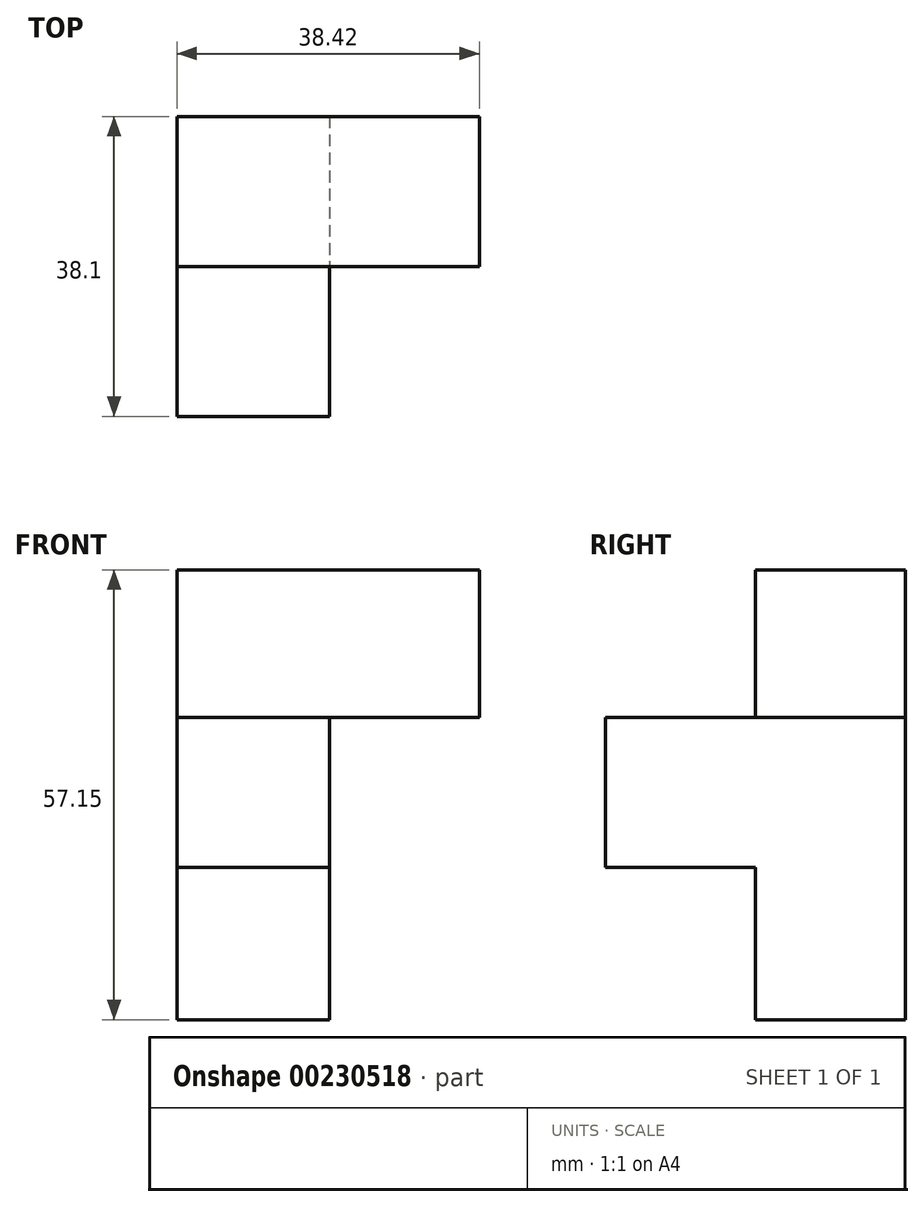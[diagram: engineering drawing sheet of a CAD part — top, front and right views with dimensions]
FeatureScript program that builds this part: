
annotation { "Feature Type Name" : "Feature", "Feature Type Description" : "" }
export const myFeature = defineFeature(function(context is Context, id is Id, definition is map)
    precondition{}
    {
        {
            var Q0;
            Q0=qCreatedBy(makeId("Top.planeOp"),FACE);
            var sketch = newSketch(context, id + "F0", { "sketchPlane" : qUnion([Q0])});
            skLineSegment(sketch, "E0.bottom", {"start": v(-19.07, -38.1) * mm, "end": v(-38.44, -38.1) * mm});
            skLineSegment(sketch, "E0.top", {"start": v(-19.07, -19.05) * mm, "end": v(-38.44, -19.05) * mm});
            skLineSegment(sketch, "E0.left", {"start": v(-19.07, -38.1) * mm, "end": v(-19.07, -19.05) * mm});
            skLineSegment(sketch, "E0.right", {"start": v(-38.44, -38.1) * mm, "end": v(-38.44, -19.05) * mm});
            skSolve(sketch);
        }
        {
            var Q0;
            Q0=makeQuery(id+"F0.imprint","IMPRINT",FACE,{"disambiguationData":[TD([[makeQuery(id+"F0.imprint","IMPRINT",EDGE,{"derivedFrom":sQuery(id+"F0.wireOp",EDGE,"E0.bottom")}),-1.0]])]});
            extrude(context, id + "F1", {"entities" : qUnion([Q0]), "depth" : 57.15 * mm});
        }
        {
            var Q0;
            Q0=makeQuery(id+"F1.opExtrude","SWEPT_FACE",FACE,{"disambiguationData":[OSD([sQuery(id+"F0.wireOp",EDGE,"E0.bottom")])]});
            var sketch = newSketch(context, id + "F2", { "sketchPlane" : qUnion([Q0])});
            skLineSegment(sketch, "E1.bottom", {"start": v(-19.07, 38.4) * mm, "end": v(-38.44, 38.4) * mm});
            skLineSegment(sketch, "E1.top", {"start": v(-19.07, 19.34) * mm, "end": v(-38.44, 19.34) * mm});
            skLineSegment(sketch, "E1.left", {"start": v(-19.07, 38.4) * mm, "end": v(-19.07, 19.34) * mm});
            skLineSegment(sketch, "E1.right", {"start": v(-38.44, 38.4) * mm, "end": v(-38.44, 19.34) * mm});
            skSolve(sketch);
        }
        {
            var Q0;
            Q0=makeQuery(id+"F2.imprint","IMPRINT",FACE,{"disambiguationData":[TD([[makeQuery(id+"F2.imprint","IMPRINT",EDGE,{"derivedFrom":sQuery(id+"F2.wireOp",EDGE,"E1.bottom")}),1.0]])]});
            extrude(context, id + "F3", {"entities" : qUnion([Q0]), "operationType" : NewBodyOperationType.ADD, "depth" : 19.05 * mm});
        }
        {
            var Q0;
            Q0=makeQuery(id+"F3.boolean.opBoolean","MERGE",FACE,{"derivedFrom":[makeQuery(id+"F1.opExtrude","SWEPT_FACE",FACE,{"disambiguationData":[OSD([sQuery(id+"F0.wireOp",EDGE,"E0.left")])]}),makeQuery(id+"F3.opExtrude","SWEPT_FACE",FACE,{"disambiguationData":[OSD([sQuery(id+"F2.wireOp",EDGE,"E1.left")])]})]});
            var sketch = newSketch(context, id + "F4", { "sketchPlane" : qUnion([Q0])});
            skLineSegment(sketch, "E2.bottom", {"start": v(-19.05, 57.15) * mm, "end": v(-38.1, 57.15) * mm});
            skLineSegment(sketch, "E2.top", {"start": v(-19.05, 38.4) * mm, "end": v(-38.1, 38.4) * mm});
            skLineSegment(sketch, "E2.left", {"start": v(-19.05, 57.15) * mm, "end": v(-19.05, 38.4) * mm});
            skLineSegment(sketch, "E2.right", {"start": v(-38.1, 57.15) * mm, "end": v(-38.1, 38.4) * mm});
            skSolve(sketch);
        }
        {
            var Q0;
            Q0=makeQuery(id+"F4.imprint","IMPRINT",FACE,{"disambiguationData":[TD([[makeQuery(id+"F4.imprint","IMPRINT",EDGE,{"derivedFrom":sQuery(id+"F4.wireOp",EDGE,"E2.bottom")}),-1.0]])]});
            extrude(context, id + "F5", {"entities" : qUnion([Q0]), "operationType" : NewBodyOperationType.ADD, "depth" : 19.05 * mm});
        }
    });
